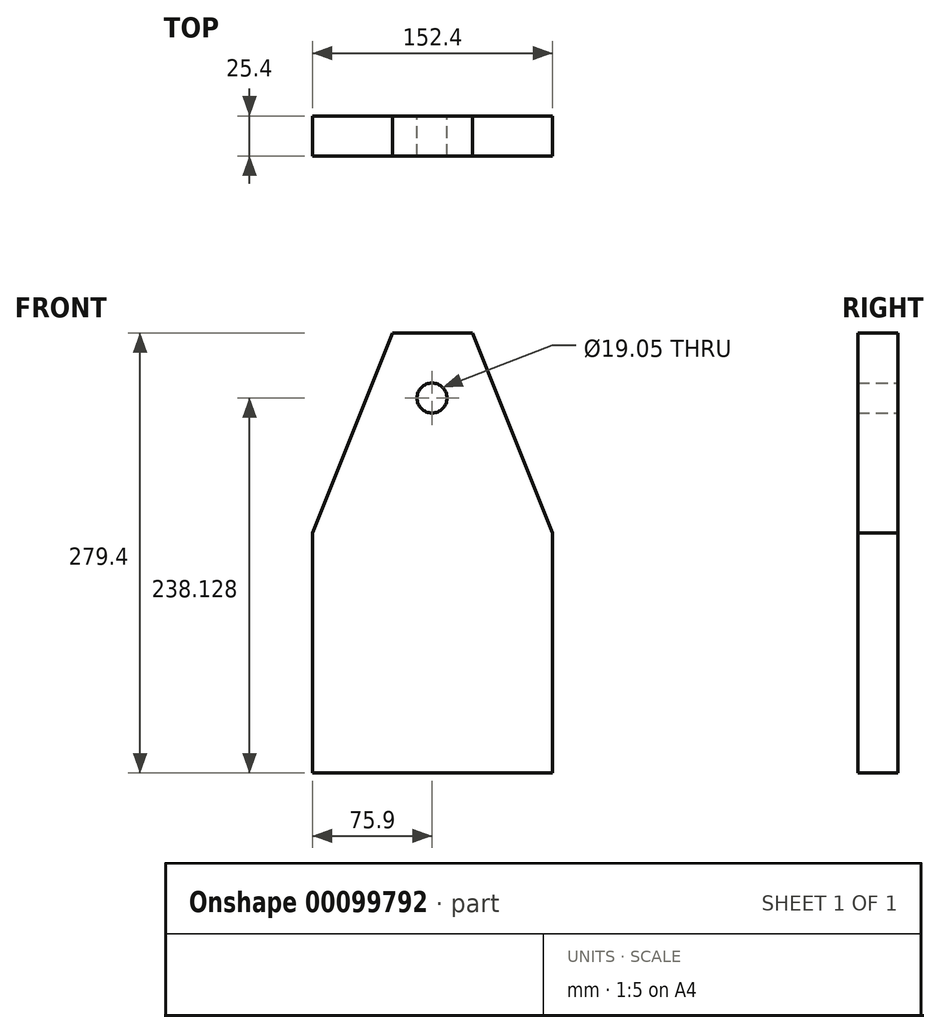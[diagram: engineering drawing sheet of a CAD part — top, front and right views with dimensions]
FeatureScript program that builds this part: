
annotation { "Feature Type Name" : "Feature", "Feature Type Description" : "" }
export const myFeature = defineFeature(function(context is Context, id is Id, definition is map)
    precondition{}
    {
        {
            var Q0;
            Q0=qCreatedBy(makeId("Front.planeOp"),FACE);
            var sketch = newSketch(context, id + "F0", { "sketchPlane" : qUnion([Q0])});
            skLineSegment(sketch, "E0", {"start": v(-75.9, -70.3) * mm, "end": v(76.5, -70.3) * mm});
            skLineSegment(sketch, "E1", {"start": v(-75.9, -70.3) * mm, "end": v(-75.9, 209.1) * mm});
            skLineSegment(sketch, "E2", {"start": v(76.5, -70.3) * mm, "end": v(76.5, 209.1) * mm});
            skLineSegment(sketch, "E3", {"start": v(-75.9, 209.1) * mm, "end": v(76.5, 209.1) * mm});
            skCircle(sketch, "E4", {"center": v(0, 167.83) * mm, "radius": 9.52 * mm});
            skSolve(sketch);
        }
        {
            var Q0;
            Q0=makeQuery(id+"F0.imprint","IMPRINT",FACE,{"disambiguationData":[TD([[makeQuery(id+"F0.imprint","IMPRINT",EDGE,{"derivedFrom":sQuery(id+"F0.wireOp",EDGE,"E0")}),1.0]])]});
            extrude(context, id + "F1", {"entities" : qUnion([Q0]), "depth" : 25.4 * mm});
        }
        {
            var Q0;
            Q0=makeQuery(id+"F1.opExtrude","SWEPT_EDGE",EDGE,{"disambiguationData":[OSD([sQuery(id+"F0.wireOp",EDGE,"E1"),sQuery(id+"F0.wireOp",EDGE,"E3")])]});
            var Q1;
            Q1=makeQuery(id+"F1.opExtrude","SWEPT_EDGE",EDGE,{"disambiguationData":[OSD([sQuery(id+"F0.wireOp",EDGE,"E2"),sQuery(id+"F0.wireOp",EDGE,"E3")])]});
            chamfer(context, id + "F2", {"entities" : qUnion([Q0, Q1]), "chamferType" : ChamferType.TWO_OFFSETS, "width1" : 127 * mm, "oppositeDirection" : false, "width2" : 50.8 * mm});
        }
    });
